# Revit family: Shower_Base-Acorn-Terrazzo_Ware-SBADA-36-3F
name_source: partatom
category: Plumbing Fixtures
units: mm (PartAtom-declared; Revit-internal decimal feet)

## family parameters
Always vertical = No
Cut with Voids When Loaded = No
OmniClass Number = 23.45.05.14.17
OmniClass Title = Showers
Part Type = Normal
Room Calculation Point = No
Round Connector Dimension = Use Diameter
Shared = Yes
Work Plane-Based = Yes

## types (1)
- SBADA-36-3F
    A-Dimension = 36 "
    ADA Compliant = Yes
    Assembly Code = D2010710
    B-Dimension = 36 "
    C-Dimension = 39 "
    CW Connection = No
    CWFU = 3
    Compliance Certifications = Terrazzo Shower Bases have Third Party Certification of conformance with
CSA B45.8/IAPMO Z403 Terrazzo, Concrete and Natural Stone Plumbing Fixtures
    Compressive Strength = 3,000 PSI
    D-Dimension = 37.5 "
    Default Elevation = 0 "
    Description = 36" x 36" ID Terrazzo ADA Shower Base
    Finish = Precast Terazzo-Acorn-White
    Flange Material = Metal-Acorn-Galvanized Steel
    HW Connection = No
    HWFU = 3
    Height = 7.5 "
    Installation Type = Floor Mounted
    KDG2Drain Gasket 2" = No
    Manufacturer = Acorn Engineering
    Material = Precast Terazzo-Acorn-White
    Model = SBADA-36-3F
    Other = 0.62 "
    Product Documentation Link = https://www.acorneng.com
    Product Page URL = https://www.acorneng.com
    Strainer Finish = Metal-Acorn-Stainless Steel
    URL = https://www.acorneng.com
    VRSVandal Resistant Strainer = No
    Vent Connection = No
    WFU = 4
    Waste Connection = Yes
    Waste Connection Diameter = 2 "
    Waste Connection Radius = 1 "

## geometry (parser evidence)
native form markers: Sweep x2
no freeform markers — native parametric forms only
